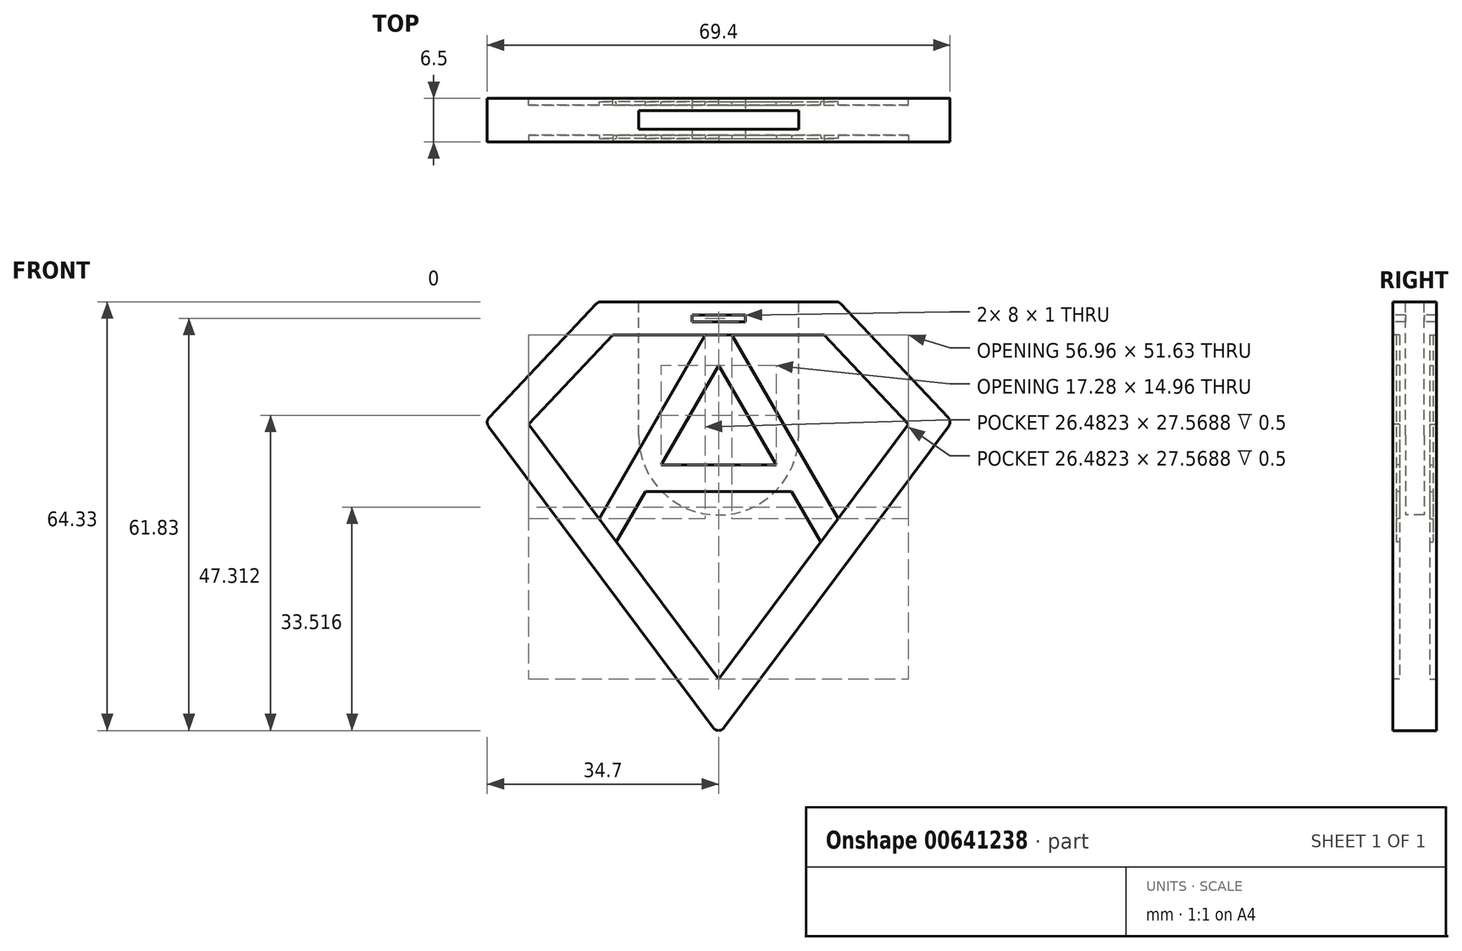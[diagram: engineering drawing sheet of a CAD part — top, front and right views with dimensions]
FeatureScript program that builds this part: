
annotation { "Feature Type Name" : "Feature", "Feature Type Description" : "" }
export const myFeature = defineFeature(function(context is Context, id is Id, definition is map)
    precondition{}
    {
        {
            var Q0;
            Q0=qCreatedBy(makeId("Front.planeOp"),FACE);
            var sketch = newSketch(context, id + "F0", { "sketchPlane" : qUnion([Q0])});
            skLineSegment(sketch, "E0", {"start": v(0, 18) * mm, "end": v(18, 18) * mm});
            skLineSegment(sketch, "E1", {"start": v(18, 18) * mm, "end": v(35, 0) * mm});
            skLineSegment(sketch, "E2", {"start": v(35, 0) * mm, "end": v(0, -47) * mm});
            skLineSegment(sketch, "E3", {"start": v(0, 18) * mm, "end": v(0, -47) * mm, "construction": true});
            skLineSegment(sketch, "E4.MirrorCS", {"start": v(-35, 0) * mm, "end": v(0, -47) * mm});
            skLineSegment(sketch, "E5.MirrorCS", {"start": v(-18, 18) * mm, "end": v(-35, 0) * mm});
            skLineSegment(sketch, "E6.MirrorCS", {"start": v(0, 18) * mm, "end": v(-18, 18) * mm});
            skSolve(sketch);
        }
        {
            var Q0;
            Q0=qSketchRegion(id+"F0",true);
            extrude(context, id + "F1", {"entities" : qUnion([Q0]), "endBound" : BoundingType.SYMMETRIC, "depth" : 6.5 * mm, "offsetDistance" : 25 * mm});
        }
        {
            var Q0;
            Q0=makeQuery(id+"F1.opExtrude","CAP_FACE",FACE,{"disambiguationData":[OSD([sQuery(id+"F0.wireOp",EDGE,"E0"),sQuery(id+"F0.wireOp",EDGE,"E1"),sQuery(id+"F0.wireOp",EDGE,"E2"),sQuery(id+"F0.wireOp",EDGE,"E4.MirrorCS"),sQuery(id+"F0.wireOp",EDGE,"E5.MirrorCS"),sQuery(id+"F0.wireOp",EDGE,"E6.MirrorCS")])],"isStart":false});
            var sketch = newSketch(context, id + "F2", { "sketchPlane" : qUnion([Q0])});
            skLineSegment(sketch, "E7.0", {"start": v(-15.84, 13) * mm, "end": v(15.84, 13) * mm});
            skLineSegment(sketch, "E8.0", {"start": v(-15.84, 13) * mm, "end": v(-28.48, -0.38) * mm});
            skLineSegment(sketch, "E9.0", {"start": v(-28.48, -0.38) * mm, "end": v(0, -38.63) * mm});
            skLineSegment(sketch, "E10.0", {"start": v(28.48, -0.38) * mm, "end": v(0, -38.63) * mm});
            skLineSegment(sketch, "E11.0", {"start": v(15.84, 13) * mm, "end": v(28.48, -0.38) * mm});
            skSolve(sketch);
        }
        {
            var Q0;
            Q0=qSketchRegion(id+"F2",true);
            extrude(context, id + "F3", {"entities" : qUnion([Q0]), "operationType" : NewBodyOperationType.REMOVE, "oppositeDirection" : true, "depth" : 0.5 * mm, "offsetDistance" : 25 * mm});
        }
        {
            var Q0;
            Q0=makeQuery(id+"F1.opExtrude","CAP_FACE",FACE,{"disambiguationData":[OSD([sQuery(id+"F0.wireOp",EDGE,"E0"),sQuery(id+"F0.wireOp",EDGE,"E1"),sQuery(id+"F0.wireOp",EDGE,"E2"),sQuery(id+"F0.wireOp",EDGE,"E4.MirrorCS"),sQuery(id+"F0.wireOp",EDGE,"E5.MirrorCS"),sQuery(id+"F0.wireOp",EDGE,"E6.MirrorCS")])],"isStart":true});
            var sketch = newSketch(context, id + "F4", { "sketchPlane" : qUnion([Q0])});
            skLineSegment(sketch, "E12.0", {"start": v(15.84, 13) * mm, "end": v(-15.84, 13) * mm});
            skLineSegment(sketch, "E13.0", {"start": v(15.84, 13) * mm, "end": v(28.48, -0.38) * mm});
            skLineSegment(sketch, "E14.0", {"start": v(28.48, -0.38) * mm, "end": v(0, -38.63) * mm});
            skLineSegment(sketch, "E15.0", {"start": v(-28.48, -0.38) * mm, "end": v(0, -38.63) * mm});
            skLineSegment(sketch, "E15.1", {"start": v(-15.84, 13) * mm, "end": v(-28.48, -0.38) * mm});
            skSolve(sketch);
        }
        {
            var Q0;
            Q0=qSketchRegion(id+"F4",true);
            extrude(context, id + "F5", {"entities" : qUnion([Q0]), "operationType" : NewBodyOperationType.REMOVE, "oppositeDirection" : true, "depth" : 0.5 * mm, "offsetDistance" : 25 * mm});
        }
        {
            var Q0;
            Q0=makeQuery(id+"F3.boolean.opBoolean","COPY",FACE,{"derivedFrom":makeQuery(id+"F3.opExtrude","CAP_FACE",FACE,{"disambiguationData":[OSD([sQuery(id+"F2.wireOp",EDGE,"E7.0"),sQuery(id+"F2.wireOp",EDGE,"E8.0"),sQuery(id+"F2.wireOp",EDGE,"E9.0"),sQuery(id+"F2.wireOp",EDGE,"E10.0"),sQuery(id+"F2.wireOp",EDGE,"E11.0")])],"isStart":false})});
            var sketch = newSketch(context, id + "F6", { "sketchPlane" : qUnion([Q0])});
            skLineSegment(sketch, "E16", {"start": v(-2, 13) * mm, "end": v(-17.92, -14.57) * mm});
            skLineSegment(sketch, "E17", {"start": v(2, 13) * mm, "end": v(17.92, -14.57) * mm});
            skLineSegment(sketch, "E18.0", {"start": v(0, 8.46) * mm, "end": v(-8.64, -6.5) * mm});
            skLineSegment(sketch, "E19.0", {"start": v(0, 8.46) * mm, "end": v(8.64, -6.5) * mm});
            skLineSegment(sketch, "E20.0", {"start": v(28.48, -0.38) * mm, "end": v(17.92, -14.57) * mm});
            skLineSegment(sketch, "E20.1", {"start": v(-28.48, -0.38) * mm, "end": v(-17.92, -14.57) * mm});
            skLineSegment(sketch, "E20.2", {"start": v(-15.84, 13) * mm, "end": v(-28.48, -0.38) * mm});
            skLineSegment(sketch, "E20.3", {"start": v(-15.84, 13) * mm, "end": v(-2, 13) * mm});
            skLineSegment(sketch, "E20.4", {"start": v(15.84, 13) * mm, "end": v(28.48, -0.38) * mm});
            skLineSegment(sketch, "E21.trimOffspring", {"start": v(2, 13) * mm, "end": v(15.84, 13) * mm});
            skLineSegment(sketch, "E22.trimOffspring", {"start": v(15.32, -18.06) * mm, "end": v(0, -38.63) * mm});
            skLineSegment(sketch, "E23.trimOffspring", {"start": v(-15.32, -18.06) * mm, "end": v(0, -38.63) * mm});
            skLineSegment(sketch, "E24", {"start": v(-10.95, -10.5) * mm, "end": v(10.95, -10.5) * mm});
            skLineSegment(sketch, "E25.0", {"start": v(-8.64, -6.5) * mm, "end": v(8.64, -6.5) * mm});
            skLineSegment(sketch, "E26.trimOffspring", {"start": v(-10.95, -10.5) * mm, "end": v(-15.32, -18.06) * mm});
            skLineSegment(sketch, "E27.trimOffspring", {"start": v(10.95, -10.5) * mm, "end": v(15.32, -18.06) * mm});
            skSolve(sketch);
        }
        {
            var Q0;
            Q0=qSketchRegion(id+"F6",true);
            extrude(context, id + "F7", {"entities" : qUnion([Q0]), "operationType" : NewBodyOperationType.REMOVE, "oppositeDirection" : true, "depth" : 0.5 * mm, "offsetDistance" : 25 * mm});
        }
        {
            var Q0;
            Q0=makeQuery(id+"F5.boolean.opBoolean","COPY",FACE,{"derivedFrom":makeQuery(id+"F5.opExtrude","CAP_FACE",FACE,{"disambiguationData":[OSD([sQuery(id+"F4.wireOp",EDGE,"E12.0"),sQuery(id+"F4.wireOp",EDGE,"E13.0"),sQuery(id+"F4.wireOp",EDGE,"E14.0"),sQuery(id+"F4.wireOp",EDGE,"E15.0"),sQuery(id+"F4.wireOp",EDGE,"E15.1")])],"isStart":false})});
            var sketch = newSketch(context, id + "F8", { "sketchPlane" : qUnion([Q0])});
            skLineSegment(sketch, "E28.0", {"start": v(15.84, 13) * mm, "end": v(28.48, -0.38) * mm});
            skLineSegment(sketch, "E28.1", {"start": v(15.84, 13) * mm, "end": v(2, 13) * mm});
            skLineSegment(sketch, "E28.2", {"start": v(-15.84, 13) * mm, "end": v(-28.48, -0.38) * mm});
            skLineSegment(sketch, "E28.3", {"start": v(-28.48, -0.38) * mm, "end": v(-17.92, -14.57) * mm});
            skLineSegment(sketch, "E28.4", {"start": v(28.48, -0.38) * mm, "end": v(17.92, -14.57) * mm});
            skLineSegment(sketch, "E28.5", {"start": v(10.95, -10.5) * mm, "end": v(15.32, -18.06) * mm});
            skLineSegment(sketch, "E28.6", {"start": v(10.95, -10.5) * mm, "end": v(-10.95, -10.5) * mm});
            skLineSegment(sketch, "E28.7", {"start": v(-10.95, -10.5) * mm, "end": v(-15.32, -18.06) * mm});
            skLineSegment(sketch, "E28.8", {"start": v(-2, 13) * mm, "end": v(-17.92, -14.57) * mm});
            skLineSegment(sketch, "E28.9", {"start": v(0, 8.46) * mm, "end": v(-8.64, -6.5) * mm});
            skLineSegment(sketch, "E28.10", {"start": v(8.64, -6.5) * mm, "end": v(-8.64, -6.5) * mm});
            skLineSegment(sketch, "E28.11", {"start": v(0, 8.46) * mm, "end": v(8.64, -6.5) * mm});
            skLineSegment(sketch, "E28.12", {"start": v(2, 13) * mm, "end": v(17.92, -14.57) * mm});
            skLineSegment(sketch, "E29.trimOffspring", {"start": v(-2, 13) * mm, "end": v(-15.84, 13) * mm});
            skLineSegment(sketch, "E30.trimOffspring", {"start": v(-15.32, -18.06) * mm, "end": v(0, -38.63) * mm});
            skLineSegment(sketch, "E31.trimOffspring", {"start": v(15.32, -18.06) * mm, "end": v(0, -38.63) * mm});
            skSolve(sketch);
        }
        {
            var Q0;
            Q0=qSketchRegion(id+"F8",true);
            extrude(context, id + "F9", {"entities" : qUnion([Q0]), "operationType" : NewBodyOperationType.REMOVE, "oppositeDirection" : true, "depth" : 0.5 * mm, "offsetDistance" : 25 * mm});
        }
        {
            var Q0;
            Q0=makeQuery(id+"F1.opExtrude","SWEPT_FACE",FACE,{"disambiguationData":[OSD([sQuery(id+"F0.wireOp",EDGE,"E0"),sQuery(id+"F0.wireOp",EDGE,"E6.MirrorCS")])]});
            var sketch = newSketch(context, id + "F10", { "sketchPlane" : qUnion([Q0])});
            skLineSegment(sketch, "E32.bottom", {"start": v(-12, 1.4) * mm, "end": v(12, 1.4) * mm});
            skLineSegment(sketch, "E32.top", {"start": v(-12, -1.4) * mm, "end": v(12, -1.4) * mm});
            skLineSegment(sketch, "E32.left", {"start": v(-12, 1.4) * mm, "end": v(-12, -1.4) * mm});
            skLineSegment(sketch, "E32.right", {"start": v(12, 1.4) * mm, "end": v(12, -1.4) * mm});
            skSolve(sketch);
        }
        {
            var Q0;
            Q0=qSketchRegion(id+"F10",true);
            extrude(context, id + "F11", {"entities" : qUnion([Q0]), "operationType" : NewBodyOperationType.REMOVE, "oppositeDirection" : true, "depth" : 20 * mm, "offsetDistance" : 25 * mm});
        }
        {
            var Q0;
            Q0=qCreatedBy(makeId("Front.planeOp"),FACE);
            var sketch = newSketch(context, id + "F12", { "sketchPlane" : qUnion([Q0])});
            skLineSegment(sketch, "E33.0", {"start": v(-12, -2) * mm, "end": v(12, -2) * mm});
            skArc(sketch, "E34", {"start": v(-12, -2) * mm, "mid": v(0, -14) * mm, "end": v(12, -2) * mm});
            skSolve(sketch);
        }
        {
            var Q0;
            Q0=qSketchRegion(id+"F12",true);
            extrude(context, id + "F13", {"entities" : qUnion([Q0]), "operationType" : NewBodyOperationType.REMOVE, "endBound" : BoundingType.SYMMETRIC, "oppositeDirection" : true, "depth" : 2.8 * mm, "offsetDistance" : 25 * mm});
        }
        {
            var Q0;
            Q0=makeQuery(id+"F1.opExtrude","CAP_FACE",FACE,{"disambiguationData":[OSD([sQuery(id+"F0.wireOp",EDGE,"E0"),sQuery(id+"F0.wireOp",EDGE,"E1"),sQuery(id+"F0.wireOp",EDGE,"E2"),sQuery(id+"F0.wireOp",EDGE,"E4.MirrorCS"),sQuery(id+"F0.wireOp",EDGE,"E5.MirrorCS"),sQuery(id+"F0.wireOp",EDGE,"E6.MirrorCS")])],"isStart":false});
            var sketch = newSketch(context, id + "F14", { "sketchPlane" : qUnion([Q0])});
            skLineSegment(sketch, "E35.bottom", {"start": v(-4, 16) * mm, "end": v(4, 16) * mm});
            skLineSegment(sketch, "E35.top", {"start": v(-4, 15) * mm, "end": v(4, 15) * mm});
            skLineSegment(sketch, "E35.left", {"start": v(-4, 16) * mm, "end": v(-4, 15) * mm});
            skLineSegment(sketch, "E35.right", {"start": v(4, 16) * mm, "end": v(4, 15) * mm});
            skSolve(sketch);
        }
        {
            var Q0;
            Q0=qSketchRegion(id+"F14",true);
            extrude(context, id + "F15", {"entities" : qUnion([Q0]), "operationType" : NewBodyOperationType.REMOVE, "oppositeDirection" : true, "depth" : 25 * mm, "offsetDistance" : 25 * mm});
        }
        {
            var Q0;
            Q0=makeQuery(id+"F1.opExtrude","SWEPT_EDGE",EDGE,{"disambiguationData":[OSD([sQuery(id+"F0.wireOp",EDGE,"E2"),sQuery(id+"F0.wireOp",EDGE,"E4.MirrorCS")])]});
            var Q1;
            Q1=makeQuery(id+"F1.opExtrude","SWEPT_EDGE",EDGE,{"disambiguationData":[OSD([sQuery(id+"F0.wireOp",EDGE,"E1"),sQuery(id+"F0.wireOp",EDGE,"E2")])]});
            var Q2;
            Q2=makeQuery(id+"F1.opExtrude","SWEPT_EDGE",EDGE,{"disambiguationData":[OSD([sQuery(id+"F0.wireOp",EDGE,"E4.MirrorCS"),sQuery(id+"F0.wireOp",EDGE,"E5.MirrorCS")])]});
            var Q3;
            Q3=makeQuery(id+"F1.opExtrude","SWEPT_EDGE",EDGE,{"disambiguationData":[OSD([sQuery(id+"F0.wireOp",EDGE,"E5.MirrorCS"),sQuery(id+"F0.wireOp",EDGE,"E6.MirrorCS")])]});
            var Q4;
            Q4=makeQuery(id+"F1.opExtrude","SWEPT_EDGE",EDGE,{"disambiguationData":[OSD([sQuery(id+"F0.wireOp",EDGE,"E0"),sQuery(id+"F0.wireOp",EDGE,"E1")])]});
            fillet(context, id + "F16", {"entities" : qUnion([Q0, Q1, Q2, Q3, Q4]), "radius" : 1 * mm, "tangentPropagation" : true, "allowEdgeOverflow" : false});
        }
    });
